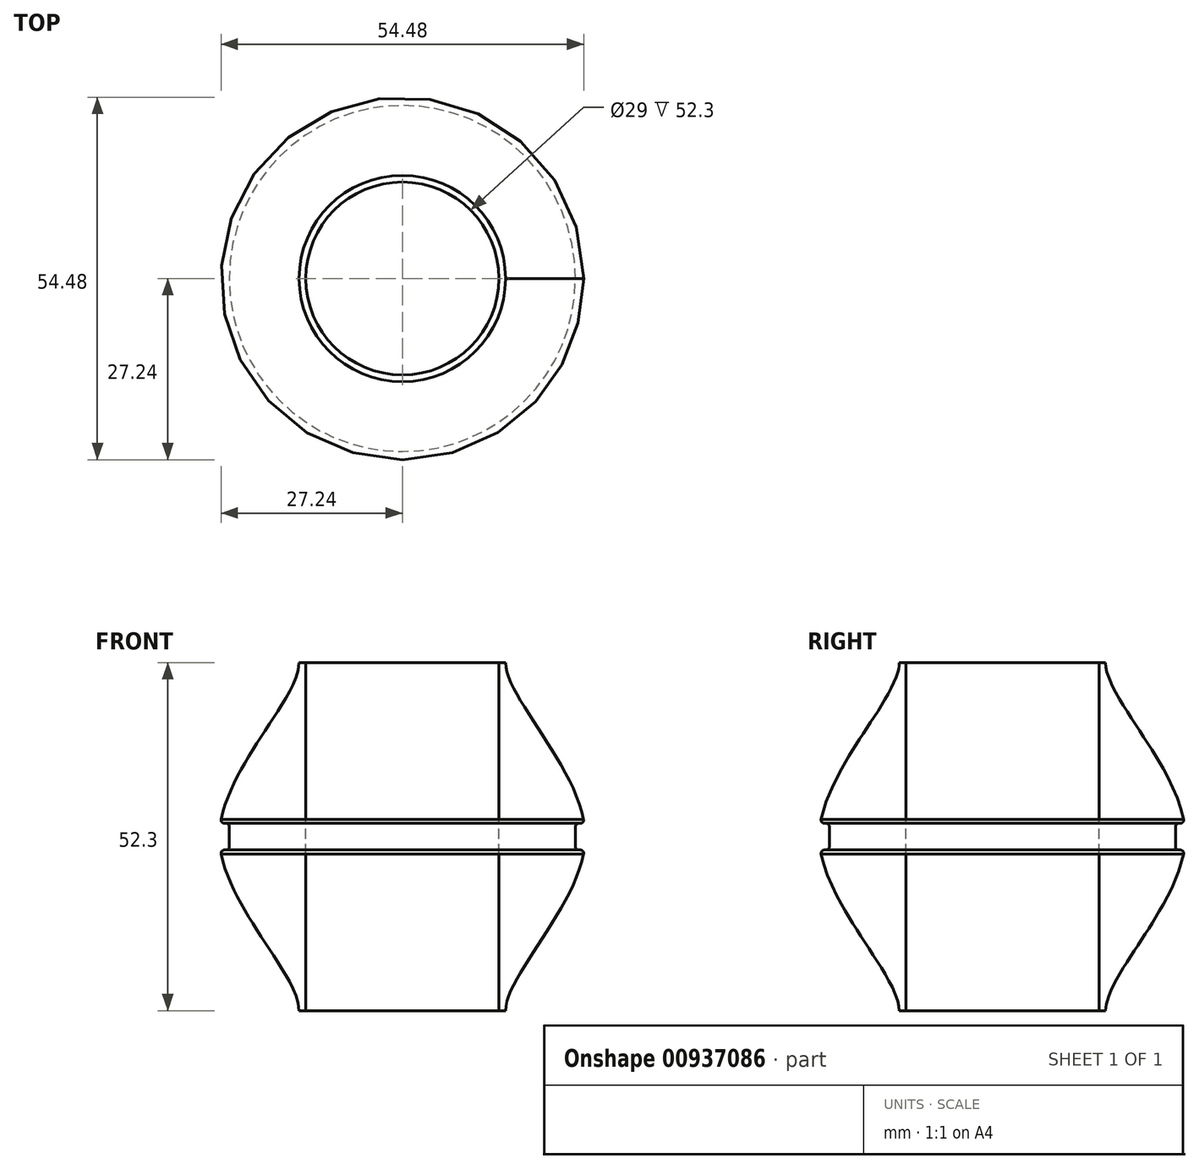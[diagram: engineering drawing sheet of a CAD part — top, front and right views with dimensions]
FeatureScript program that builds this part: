
annotation { "Feature Type Name" : "Feature", "Feature Type Description" : "" }
export const myFeature = defineFeature(function(context is Context, id is Id, definition is map)
    precondition{}
    {
        {
            var Q0;
            Q0=qCreatedBy(makeId("Right.planeOp"),FACE);
            var sketch = newSketch(context, id + "F0", { "sketchPlane" : qUnion([Q0])});
            skLineSegment(sketch, "E0.bottom", {"start": v(15.5, 26.15) * mm, "end": v(-15.5, 26.15) * mm});
            skLineSegment(sketch, "E0.top", {"start": v(15.5, -26.15) * mm, "end": v(-15.5, -26.15) * mm});
            skLineSegment(sketch, "E0.left", {"start": v(15.5, 26.15) * mm, "end": v(15.5, -26.15) * mm});
            skLineSegment(sketch, "E0.right", {"start": v(-15.5, 26.15) * mm, "end": v(-15.5, -26.15) * mm});
            skPoint(sketch, "E0.middle", {"position": v(0, 0) * mm});
            skLineSegment(sketch, "E1.bottom", {"start": v(14.5, -26.15) * mm, "end": v(-14.5, -26.15) * mm});
            skLineSegment(sketch, "E1.top", {"start": v(14.5, 26.15) * mm, "end": v(-14.5, 26.15) * mm});
            skLineSegment(sketch, "E1.left", {"start": v(14.5, -26.15) * mm, "end": v(14.5, 26.15) * mm});
            skLineSegment(sketch, "E1.right", {"start": v(-14.5, -26.15) * mm, "end": v(-14.5, 26.15) * mm});
            skLineSegment(sketch, "E2", {"start": v(-15.5, 0) * mm, "end": v(-27.5, 0) * mm});
            skFitSpline(sketch, "E3", {"points": [v(-15.5, 26.15) * mm, v(-27.5, 0) * mm], "startDerivative": vector(0, -16.5) * mm, "endDerivative": vector(0, -28.5) * mm});
            skFitSpline(sketch, "E4", {"points": [v(-27.5, 0) * mm, v(-15.5, -26.15) * mm], "startDerivative": vector(0, -28.5) * mm, "endDerivative": vector(0, -16.5) * mm});
            skLineSegment(sketch, "E5", {"start": v(0, 36.46) * mm, "end": v(0, -33.85) * mm, "construction": true});
            skLineSegment(sketch, "E6.bottom", {"start": v(-26.5, -2) * mm, "end": v(-29, -2) * mm});
            skLineSegment(sketch, "E6.top", {"start": v(-26.5, 2) * mm, "end": v(-29, 2) * mm});
            skLineSegment(sketch, "E6.left", {"start": v(-26, -1.5) * mm, "end": v(-26, 1.5) * mm});
            skLineSegment(sketch, "E6.right", {"start": v(-29, -2) * mm, "end": v(-29, 2) * mm});
            skPoint(sketch, "E7.visualSharp", {"position": v(-26, 2) * mm});
            skArc(sketch, "E7.filletArc", {"start": v(-26, 1.5) * mm, "mid": v(-26.15, 1.85) * mm, "end": v(-26.5, 2) * mm});
            skPoint(sketch, "E8.visualSharp", {"position": v(-26, -2) * mm});
            skArc(sketch, "E8.filletArc", {"start": v(-26.5, -2) * mm, "mid": v(-26.15, -1.85) * mm, "end": v(-26, -1.5) * mm});
            skSolve(sketch);
        }
        {
            var Q0;
            {var subQ6=sQuery(id+"F0.wireOp",EDGE,"E1.right");Q0=makeQuery(id+"F0.imprint","IMPRINT",FACE,{"disambiguationData":[TD([[makeQuery(id+"F0.imprint","IMPRINT",EDGE,{"derivedFrom":subQ6}),1.0]])]});}
            var Q1;
            {var subQ0=sQuery(id+"F0.wireOp",EDGE,"E7.filletArc");Q1=makeQuery(id+"F0.imprint","IMPRINT",FACE,{"disambiguationData":[TD([[makeQuery(id+"F0.imprint","IMPRINT",EDGE,{"derivedFrom":subQ0}),-1.0]])]});}
            var Q2;
            {var subQ0=sQuery(id+"F0.wireOp",EDGE,"E8.filletArc");Q2=makeQuery(id+"F0.imprint","IMPRINT",FACE,{"disambiguationData":[TD([[makeQuery(id+"F0.imprint","IMPRINT",EDGE,{"derivedFrom":subQ0}),-1.0]])]});}
            var Q3;
            Q3=sQuery(id+"F0.wireOp",EDGE,"E5");
            revolve(context, id + "F1", {"surfaceOperationType" : NewSurfaceOperationType.NEW, "entities" : qUnion([Q0, Q1, Q2]), "axis" : qUnion([Q3]), "revolveType" : RevolveType.FULL});
        }
        {
            var Q0;
            Q0=makeQuery(id+"F1.opRevolve","SWEPT_EDGE",EDGE,{"disambiguationData":[OSD([sQuery(id+"F0.wireOp",EDGE,"E4"),sQuery(id+"F0.wireOp",EDGE,"E6.bottom")])]});
            var Q1;
            Q1=makeQuery(id+"F1.opRevolve","SWEPT_EDGE",EDGE,{"disambiguationData":[OSD([sQuery(id+"F0.wireOp",EDGE,"E3"),sQuery(id+"F0.wireOp",EDGE,"E6.top")])]});
            fillet(context, id + "F2", {"entities" : qUnion([Q0, Q1]), "radius" : .5 * mm, "tangentPropagation" : true, "allowEdgeOverflow" : false});
        }
    });
